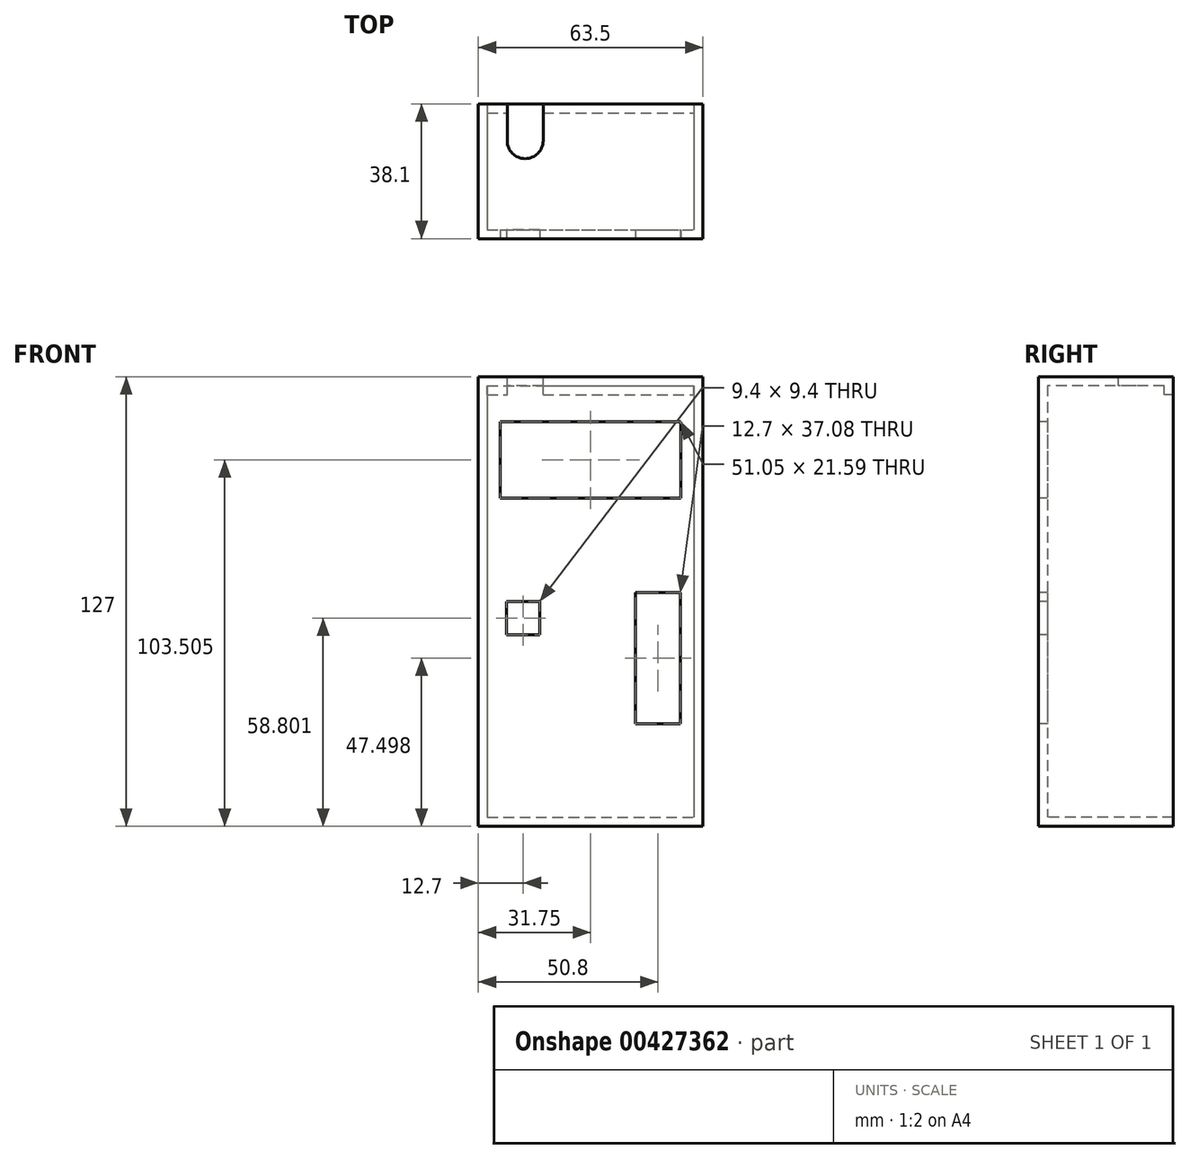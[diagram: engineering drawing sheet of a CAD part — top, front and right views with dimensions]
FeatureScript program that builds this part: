
annotation { "Feature Type Name" : "Feature", "Feature Type Description" : "" }
export const myFeature = defineFeature(function(context is Context, id is Id, definition is map)
    precondition{}
    {
        {
            var Q0;
            Q0=qCreatedBy(makeId("Front.planeOp"),FACE);
            var sketch = newSketch(context, id + "F0", { "sketchPlane" : qUnion([Q0])});
            skLineSegment(sketch, "E0.bottom", {"start": v(-31.75, 63.5) * mm, "end": v(31.75, 63.5) * mm});
            skLineSegment(sketch, "E0.top", {"start": v(-31.75, -63.5) * mm, "end": v(31.75, -63.5) * mm});
            skLineSegment(sketch, "E0.left", {"start": v(-31.75, 63.5) * mm, "end": v(-31.75, -63.5) * mm});
            skLineSegment(sketch, "E0.right", {"start": v(31.75, 63.5) * mm, "end": v(31.75, -63.5) * mm});
            skLineSegment(sketch, "E1.bottom", {"start": v(-25.53, 50.8) * mm, "end": v(25.53, 50.8) * mm});
            skLineSegment(sketch, "E1.top", {"start": v(-25.53, 29.21) * mm, "end": v(25.53, 29.21) * mm});
            skLineSegment(sketch, "E1.left", {"start": v(-25.53, 50.8) * mm, "end": v(-25.53, 29.21) * mm});
            skLineSegment(sketch, "E1.right", {"start": v(25.53, 50.8) * mm, "end": v(25.53, 29.21) * mm});
            skLineSegment(sketch, "E2", {"start": v(0, 63.5) * mm, "end": v(0, -63.5) * mm, "construction": true});
            skLineSegment(sketch, "E3", {"start": v(-25.53, 40) * mm, "end": v(25.53, 40) * mm, "construction": true});
            skPoint(sketch, "E4", {"position": v(0, 40) * mm});
            skLineSegment(sketch, "E5", {"start": v(19.05, -63.5) * mm, "end": v(19.05, 63.5) * mm, "construction": true});
            skLineSegment(sketch, "E6.0", {"start": v(-29.2, 60.96) * mm, "end": v(29.21, 60.96) * mm});
            skLineSegment(sketch, "E6.1", {"start": v(-29.2, 60.96) * mm, "end": v(-29.2, -60.96) * mm});
            skLineSegment(sketch, "E6.2", {"start": v(-29.2, -60.96) * mm, "end": v(29.21, -60.96) * mm});
            skLineSegment(sketch, "E6.3", {"start": v(29.21, 60.96) * mm, "end": v(29.2, -60.96) * mm});
            skLineSegment(sketch, "E7.bottom", {"start": v(-14.35, 0) * mm, "end": v(-23.75, 0) * mm});
            skLineSegment(sketch, "E7.top", {"start": v(-14.35, -9.4) * mm, "end": v(-23.75, -9.4) * mm});
            skLineSegment(sketch, "E7.left", {"start": v(-14.35, 0) * mm, "end": v(-14.35, -9.4) * mm});
            skLineSegment(sketch, "E7.right", {"start": v(-23.75, 0) * mm, "end": v(-23.75, -9.4) * mm});
            skPoint(sketch, "E7.middle", {"position": v(-19.05, -4.7) * mm});
            skLineSegment(sketch, "E8.bottom", {"start": v(12.7, 2.54) * mm, "end": v(25.4, 2.54) * mm});
            skLineSegment(sketch, "E8.top", {"start": v(12.7, -34.54) * mm, "end": v(25.4, -34.54) * mm});
            skLineSegment(sketch, "E8.left", {"start": v(12.7, 2.54) * mm, "end": v(12.7, -34.54) * mm});
            skLineSegment(sketch, "E8.right", {"start": v(25.4, 2.54) * mm, "end": v(25.4, -34.54) * mm});
            skPoint(sketch, "E8.middle", {"position": v(19.05, -16) * mm});
            skSolve(sketch);
        }
        {
            var Q0;
            Q0=makeQuery(id+"F0.imprint","IMPRINT",FACE,{"disambiguationData":[TD([[makeQuery(id+"F0.imprint","IMPRINT",EDGE,{"derivedFrom":sQuery(id+"F0.wireOp",EDGE,"E0.bottom")}),-1.0]])]});
            var Q1;
            Q1=makeQuery(id+"F0.imprint","IMPRINT",FACE,{"disambiguationData":[TD([[makeQuery(id+"F0.imprint","IMPRINT",EDGE,{"derivedFrom":sQuery(id+"F0.wireOp",EDGE,"E1.bottom")}),1.0]])]});
            extrude(context, id + "F1", {"entities" : qUnion([Q0, Q1]), "oppositeDirection" : true, "depth" : 2.54 * mm, "offsetDistance" : 25.4 * mm});
        }
        {
            var Q0;
            Q0=makeQuery(id+"F0.imprint","IMPRINT",FACE,{"disambiguationData":[TD([[makeQuery(id+"F0.imprint","IMPRINT",EDGE,{"derivedFrom":sQuery(id+"F0.wireOp",EDGE,"E0.bottom")}),-1.0]])]});
            extrude(context, id + "F2", {"entities" : qUnion([Q0]), "operationType" : NewBodyOperationType.ADD, "oppositeDirection" : true, "depth" : 38.1 * mm, "offsetDistance" : 25.4 * mm});
        }
        {
            var Q0;
            Q0=makeQuery(id+"F2.opExtrude","SWEPT_FACE",FACE,{"disambiguationData":[OSD([sQuery(id+"F0.wireOp",EDGE,"E6.0")])]});
            var sketch = newSketch(context, id + "F3", { "sketchPlane" : qUnion([Q0])});
            skLineSegment(sketch, "E9.bottom", {"start": v(-29.2, -38.1) * mm, "end": v(29.2, -38.1) * mm});
            skLineSegment(sketch, "E9.top", {"start": v(-29.2, -35.56) * mm, "end": v(29.2, -35.56) * mm});
            skLineSegment(sketch, "E9.left", {"start": v(-29.2, -38.1) * mm, "end": v(-29.2, -35.56) * mm});
            skLineSegment(sketch, "E9.right", {"start": v(29.2, -38.1) * mm, "end": v(29.2, -35.56) * mm});
            skSolve(sketch);
        }
        {
            var Q0;
            Q0 = qSketchRegion(id + "F3", true);
            extrude(context, id + "F4", {"entities" : qUnion([Q0]), "operationType" : NewBodyOperationType.ADD, "depth" : 2.54 * mm, "offsetDistance" : 25.4 * mm});
        }
        {
            var Q0;
            {var subQ0=sQuery(id+"F0.wireOp",EDGE,"E0.bottom");Q0=makeQuery(id+"F2.boolean.opBoolean","MERGE",FACE,{"derivedFrom":[makeQuery(id+"F1.opExtrude","SWEPT_FACE",FACE,{"disambiguationData":[OSD([subQ0])]}),makeQuery(id+"F2.opExtrude","SWEPT_FACE",FACE,{"disambiguationData":[OSD([subQ0])]})]});}
            var sketch = newSketch(context, id + "F5", { "sketchPlane" : qUnion([Q0])});
            skLineSegment(sketch, "E10", {"start": v(-18.5, 27.71) * mm, "end": v(-18.5, 38.1) * mm, "construction": true});
            skCircle(sketch, "E11", {"center": v(-18.5, 27.71) * mm, "radius": 5.08 * mm});
            skLineSegment(sketch, "E12", {"start": v(-23.57, 27.71) * mm, "end": v(-23.57, 38.1) * mm});
            skLineSegment(sketch, "E13", {"start": v(-13.41, 27.71) * mm, "end": v(-13.41, 38.1) * mm});
            skSolve(sketch);
        }
        {
            var Q0;
            Q0 = qSketchRegion(id + "F5", true);
            var Q1;
            {var subQ0=sQuery(id+"F5.wireOp",EDGE,"E12");Q1=makeQuery(id+"F5.imprint","IMPRINT",FACE,{"disambiguationData":[TD([[makeQuery(id+"F5.imprint","IMPRINT",EDGE,{"derivedFrom":subQ0}),-1.0]])]});}
            extrude(context, id + "F6", {"entities" : qUnion([Q0, Q1]), "operationType" : NewBodyOperationType.REMOVE, "oppositeDirection" : true, "depth" : 12.1 * mm, "offsetDistance" : 25.4 * mm});
        }
    });
